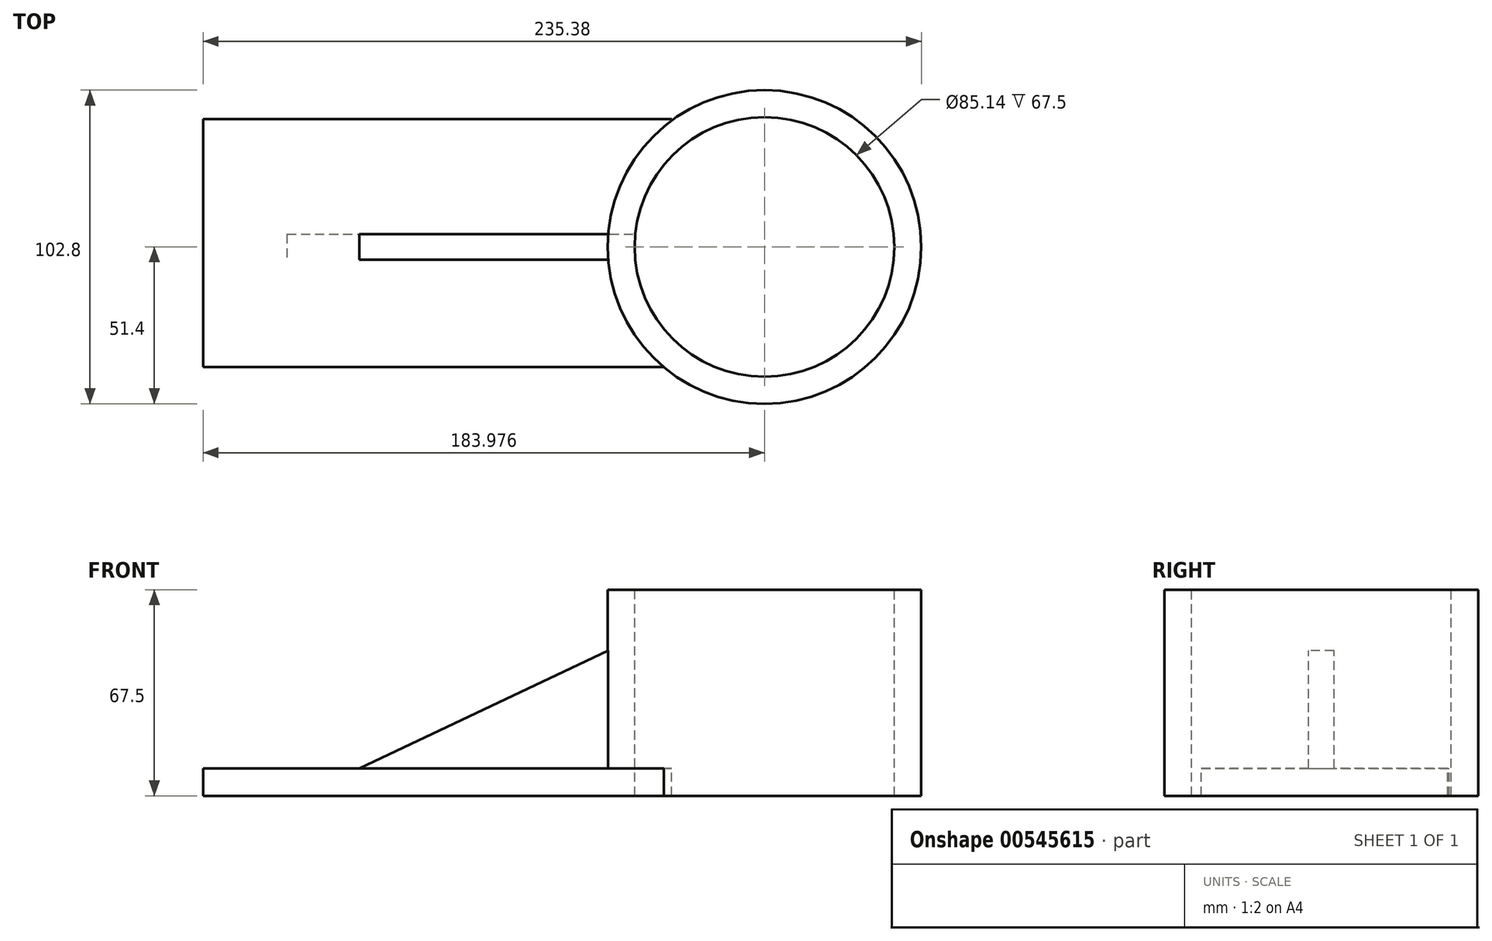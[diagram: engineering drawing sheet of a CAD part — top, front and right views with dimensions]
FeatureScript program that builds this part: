
annotation { "Feature Type Name" : "Feature", "Feature Type Description" : "" }
export const myFeature = defineFeature(function(context is Context, id is Id, definition is map)
    precondition{}
    {
        {
            var Q0;
            Q0=qCreatedBy(makeId("Front.planeOp"),FACE);
            var sketch = newSketch(context, id + "F0", { "sketchPlane" : qUnion([Q0])});
            skLineSegment(sketch, "E0.bottom", {"start": v(-87.2, -11.2) * mm, "end": v(91.78, -11.2) * mm});
            skLineSegment(sketch, "E0.top", {"start": v(-87.2, -25.06) * mm, "end": v(91.78, -25.06) * mm});
            skLineSegment(sketch, "E0.left", {"start": v(-87.2, -11.2) * mm, "end": v(-87.2, -25.06) * mm});
            skLineSegment(sketch, "E0.right", {"start": v(91.78, -11.2) * mm, "end": v(91.78, -25.06) * mm});
            skLineSegment(sketch, "E1", {"start": v(-64.44, -11.2) * mm, "end": v(55.7, 45.68) * mm});
            skLineSegment(sketch, "E2", {"start": v(55.7, 45.68) * mm, "end": v(55.7, -11.2) * mm});
            skSolve(sketch);
        }
        {
            var Q0;
            Q0=qCreatedBy(makeId("Top.planeOp"),FACE);
            var sketch = newSketch(context, id + "F1", { "sketchPlane" : qUnion([Q0])});
            skCircle(sketch, "E3", {"center": v(92.07, 0) * mm, "radius": 42.57 * mm});
            skCircle(sketch, "E4", {"center": v(92.07, 0) * mm, "radius": 51.4 * mm});
            skSolve(sketch);
        }
        {
            var Q0;
            Q0 = qSketchRegion(id + "F1", true);
            extrude(context, id + "F2", {"entities" : qUnion([Q0]), "oppositeDirection" : true, "depth" : 9 * mm, "offsetDistance" : 25 * mm});
        }
        {
            var Q0;
            Q0 = qSketchRegion(id + "F1", true);
            extrude(context, id + "F3", {"entities" : qUnion([Q0]), "operationType" : NewBodyOperationType.ADD, "depth" : 58.5 * mm, "offsetDistance" : 25 * mm});
        }
        {
            var Q0;
            {var subQ0=sQuery(id+"F0.wireOp",EDGE,"E1");Q0=makeQuery(id+"F0.imprint","IMPRINT",FACE,{"disambiguationData":[TD([[makeQuery(id+"F0.imprint","IMPRINT",EDGE,{"derivedFrom":subQ0}),-1.0]])]});}
            extrude(context, id + "F4", {"entities" : qUnion([Q0]), "operationType" : NewBodyOperationType.ADD, "depth" : 8.3 * mm, "offsetDistance" : 25 * mm, "symmetric" : true});
        }
        {
            var Q0;
            Q0=qCreatedBy(makeId("Top.planeOp"),FACE);
            var sketch = newSketch(context, id + "F5", { "sketchPlane" : qUnion([Q0])});
            skLineSegment(sketch, "E5.bottom", {"start": v(-91.9, -39.37) * mm, "end": v(61.58, -39.37) * mm});
            skLineSegment(sketch, "E5.top", {"start": v(-91.9, 41.95) * mm, "end": v(61.58, 41.95) * mm});
            skLineSegment(sketch, "E5.left", {"start": v(-91.9, -39.37) * mm, "end": v(-91.9, 41.95) * mm});
            skLineSegment(sketch, "E5.right", {"start": v(61.58, -39.37) * mm, "end": v(61.58, 41.95) * mm});
            skSolve(sketch);
        }
        {
            var Q0;
            Q0=makeQuery(id+"F5.imprint","IMPRINT",FACE,{"disambiguationData":[TD([[makeQuery(id+"F5.imprint","IMPRINT",EDGE,{"derivedFrom":sQuery(id+"F5.wireOp",EDGE,"E5.bottom")}),1.0]])]});
            extrude(context, id + "F6", {"entities" : qUnion([Q0]), "operationType" : NewBodyOperationType.ADD, "oppositeDirection" : true, "depth" : 9 * mm, "offsetDistance" : 25 * mm});
        }
        {
            var Q0;
            {var subQ3=sQuery(id+"F1.wireOp",EDGE,"E3");var subQ4=sQuery(id+"F5.wireOp",EDGE,"E5.right");Q0=makeQuery(id+"F6.boolean.opBoolean","SPLIT",FACE,{"disambiguationData":[TD([makeQuery(id+"F2.opExtrude","SWEPT_FACE",FACE,{"disambiguationData":[OSD([subQ3])]})])],"derivedFrom":makeQuery(id+"F6.opExtrude","CAP_FACE",FACE,{"disambiguationData":[OSD([sQuery(id+"F5.wireOp",EDGE,"E5.bottom"),sQuery(id+"F5.wireOp",EDGE,"E5.top"),sQuery(id+"F5.wireOp",EDGE,"E5.left"),subQ4])],"isStart":true})});}
            var Q1;
            {var subQ1=sQuery(id+"F0.wireOp",EDGE,"E1");var subQ3=sQuery(id+"F1.wireOp",EDGE,"E3");Q1=makeQuery(id+"F4.boolean.opBoolean","SPLIT",FACE,{"disambiguationData":[TD([makeQuery(id+"F2.opExtrude","SWEPT_FACE",FACE,{"disambiguationData":[OSD([subQ3])]})])],"derivedFrom":makeQuery(id+"F4.opExtrude","SWEPT_FACE",FACE,{"disambiguationData":[OSD([subQ1])]})});}
            extrude(context, id + "F7", {"entities" : qUnion([Q0, Q1]), "operationType" : NewBodyOperationType.REMOVE, "oppositeDirection" : true, "depth" : 81.9 * mm, "offsetDistance" : 25 * mm});
        }
        {
            var Q0;
            Q0=makeQuery(id+"F4.opExtrude","SWEPT_FACE",FACE,{"disambiguationData":[OSD([sQuery(id+"F0.wireOp",EDGE,"E0.bottom")])]});
            extrude(context, id + "F8", {"entities" : qUnion([Q0]), "operationType" : NewBodyOperationType.REMOVE, "oppositeDirection" : true, "depth" : 2.2 * mm, "offsetDistance" : 25 * mm});
        }
    });
